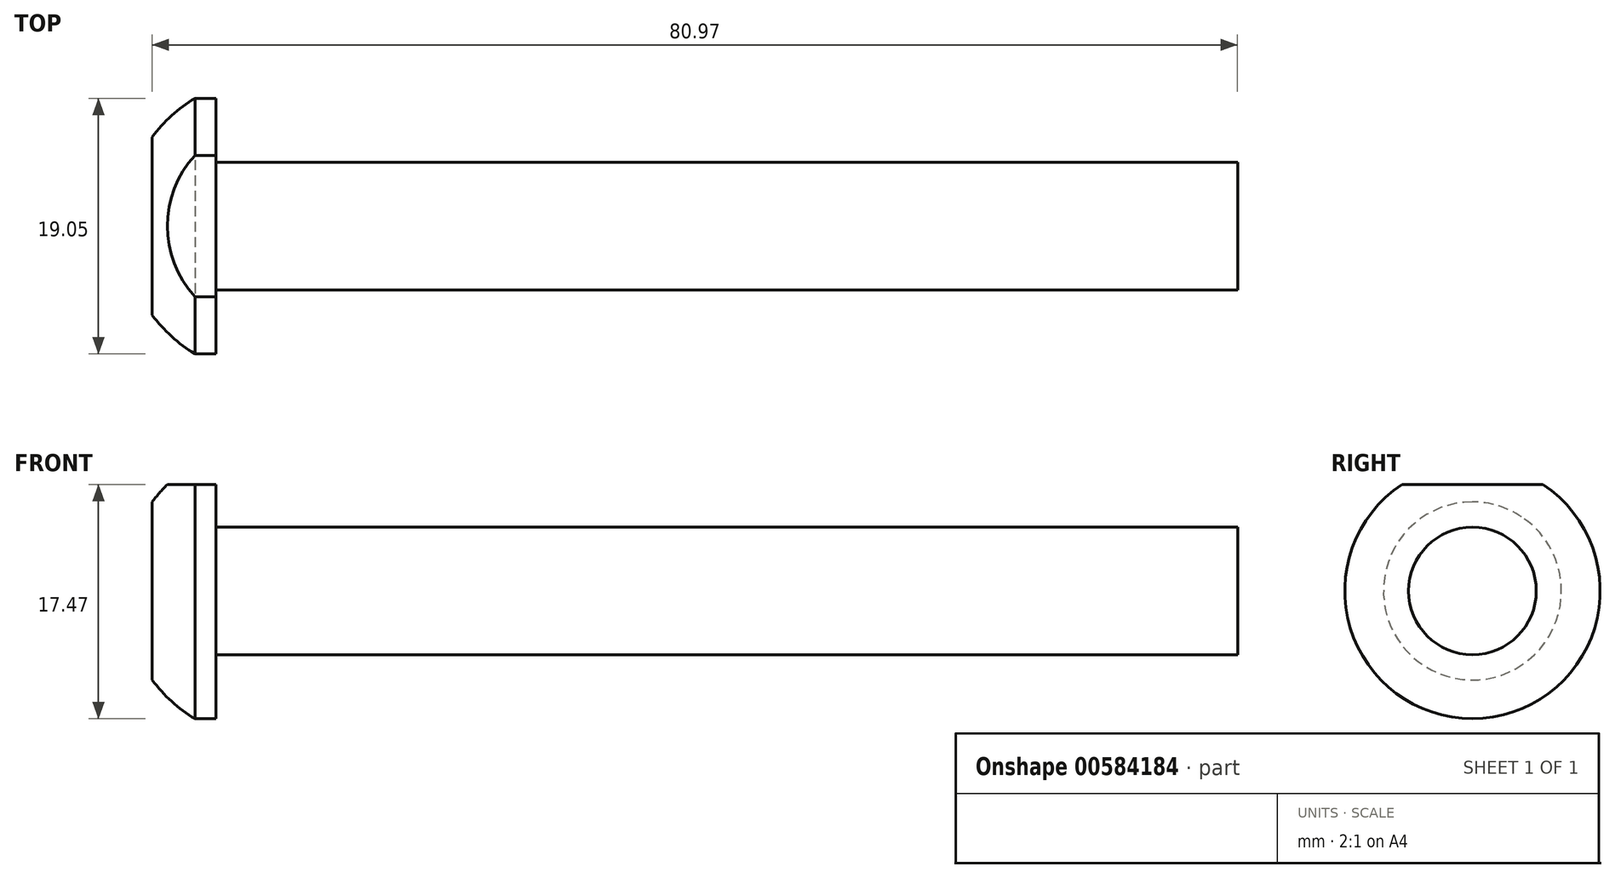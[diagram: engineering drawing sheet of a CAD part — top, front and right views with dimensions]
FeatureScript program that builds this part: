
annotation { "Feature Type Name" : "Feature", "Feature Type Description" : "" }
export const myFeature = defineFeature(function(context is Context, id is Id, definition is map)
    precondition{}
    {
        {
            var Q0;
            Q0=qCreatedBy(makeId("Top.planeOp"),FACE);
            var sketch = newSketch(context, id + "F0", { "sketchPlane" : qUnion([Q0])});
            skLineSegment(sketch, "E0.bottom", {"start": v(0, 9.67) * mm, "end": v(76.21, 9.67) * mm});
            skLineSegment(sketch, "E0.top", {"start": v(0, 14.43) * mm, "end": v(76.21, 14.43) * mm});
            skLineSegment(sketch, "E0.right", {"start": v(76.21, 9.67) * mm, "end": v(76.21, 14.43) * mm});
            skLineSegment(sketch, "E1", {"start": v(0, 14.43) * mm, "end": v(0, 19.2) * mm});
            skLineSegment(sketch, "E2", {"start": v(0, 19.2) * mm, "end": v(-1.57, 19.2) * mm});
            skArc(sketch, "E3", {"start": v(-1.57, 19.2) * mm, "mid": v(-3.3, 17.9) * mm, "end": v(-4.76, 16.3) * mm});
            skLineSegment(sketch, "E4", {"start": v(0, 9.67) * mm, "end": v(-4.76, 9.67) * mm});
            skLineSegment(sketch, "E5", {"start": v(-4.76, 9.67) * mm, "end": v(-4.76, 16.3) * mm});
            skSolve(sketch);
        }
        {
            var Q0;
            Q0=makeQuery(id+"F0.imprint","IMPRINT",FACE,{"disambiguationData":[TD([[makeQuery(id+"F0.imprint","IMPRINT",EDGE,{"derivedFrom":sQuery(id+"F0.wireOp",EDGE,"E0.bottom")}),1.0]])]});
            var Q1;
            Q1=sQuery(id+"F0.wireOp",EDGE,"E0.bottom");
            revolve(context, id + "F1", {"entities" : qUnion([Q0]), "axis" : qUnion([Q1]), "revolveType" : RevolveType.FULL});
        }
        {
            var Q0;
            Q0=makeQuery(id+"F1.opRevolve","SWEPT_FACE",FACE,{"disambiguationData":[OSD([sQuery(id+"F0.wireOp",EDGE,"E5")])]});
            var sketch = newSketch(context, id + "F2", { "sketchPlane" : qUnion([Q0])});
            skLineSegment(sketch, "E6.top", {"start": v(-22.37, 14.37) * mm, "end": v(2.33, 14.37) * mm});
            skLineSegment(sketch, "E6.left", {"start": v(-22.37, 7.94) * mm, "end": v(-22.37, 14.37) * mm});
            skLineSegment(sketch, "E6.right", {"start": v(2.33, 7.94) * mm, "end": v(2.33, 14.37) * mm});
            skPoint(sketch, "E7.start.orphan", {"position": v(-9.67, 0) * mm});
            skLineSegment(sketch, "E8", {"start": v(2.33, 7.94) * mm, "end": v(-22.37, 7.94) * mm});
            skSolve(sketch);
        }
        {
            var Q0;
            Q0=qSketchRegion(id+"F2",true);
            extrude(context, id + "F3", {"entities" : qUnion([Q0]), "operationType" : NewBodyOperationType.REMOVE, "oppositeDirection" : true, "depth" : 25.4 * mm});
        }
    });
